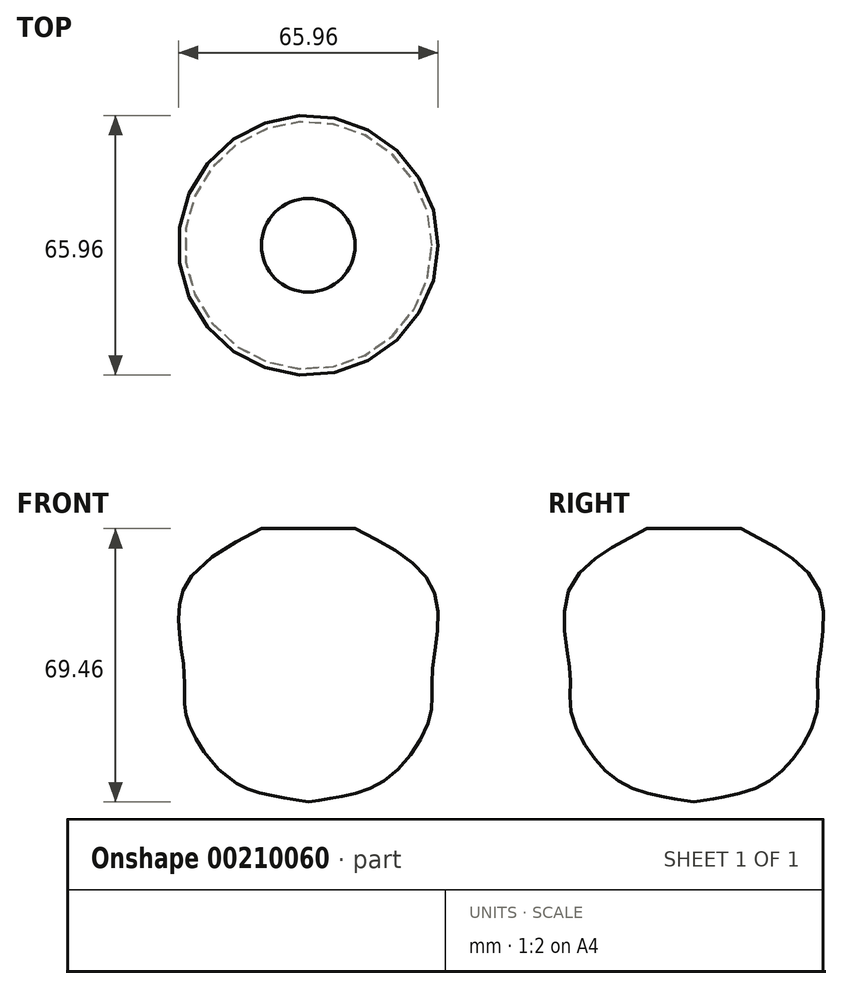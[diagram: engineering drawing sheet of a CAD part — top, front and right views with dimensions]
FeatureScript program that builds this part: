
annotation { "Feature Type Name" : "Feature", "Feature Type Description" : "" }
export const myFeature = defineFeature(function(context is Context, id is Id, definition is map)
    precondition{}
    {
        {
            var Q0;
            Q0=qCreatedBy(makeId("Front.planeOp"),FACE);
            var sketch = newSketch(context, id + "F0", { "sketchPlane" : qUnion([Q0])});
            skFitSpline(sketch, "E0", {"points": [v(11.9, 47.78) * mm, v(31.93, 31.86) * mm, v(31.46, 10.9) * mm, v(30.94, 0) * mm, v(20.03, -15.78) * mm, v(7.54, -20.38) * mm, v(0, -21.68) * mm], "startDerivative": vector(122.07, -62.06) * mm, "endDerivative": vector(-60.63, -10.3) * mm});
            skLineSegment(sketch, "E1", {"start": v(0, 63.73) * mm, "end": v(0, 50.16) * mm});
            skSolve(sketch);
        }
        {
            var Q0;
            Q0=sQuery(id+"F0.wireOp",EDGE,"E0");
            var Q1;
            Q1=sQuery(id+"F0.wireOp",EDGE,"E1");
            revolve(context, id + "F1", {"bodyType" : ToolBodyType.SURFACE, "surfaceEntities" : qUnion([Q0]), "axis" : qUnion([Q1]), "revolveType" : RevolveType.FULL});
        }
    });
